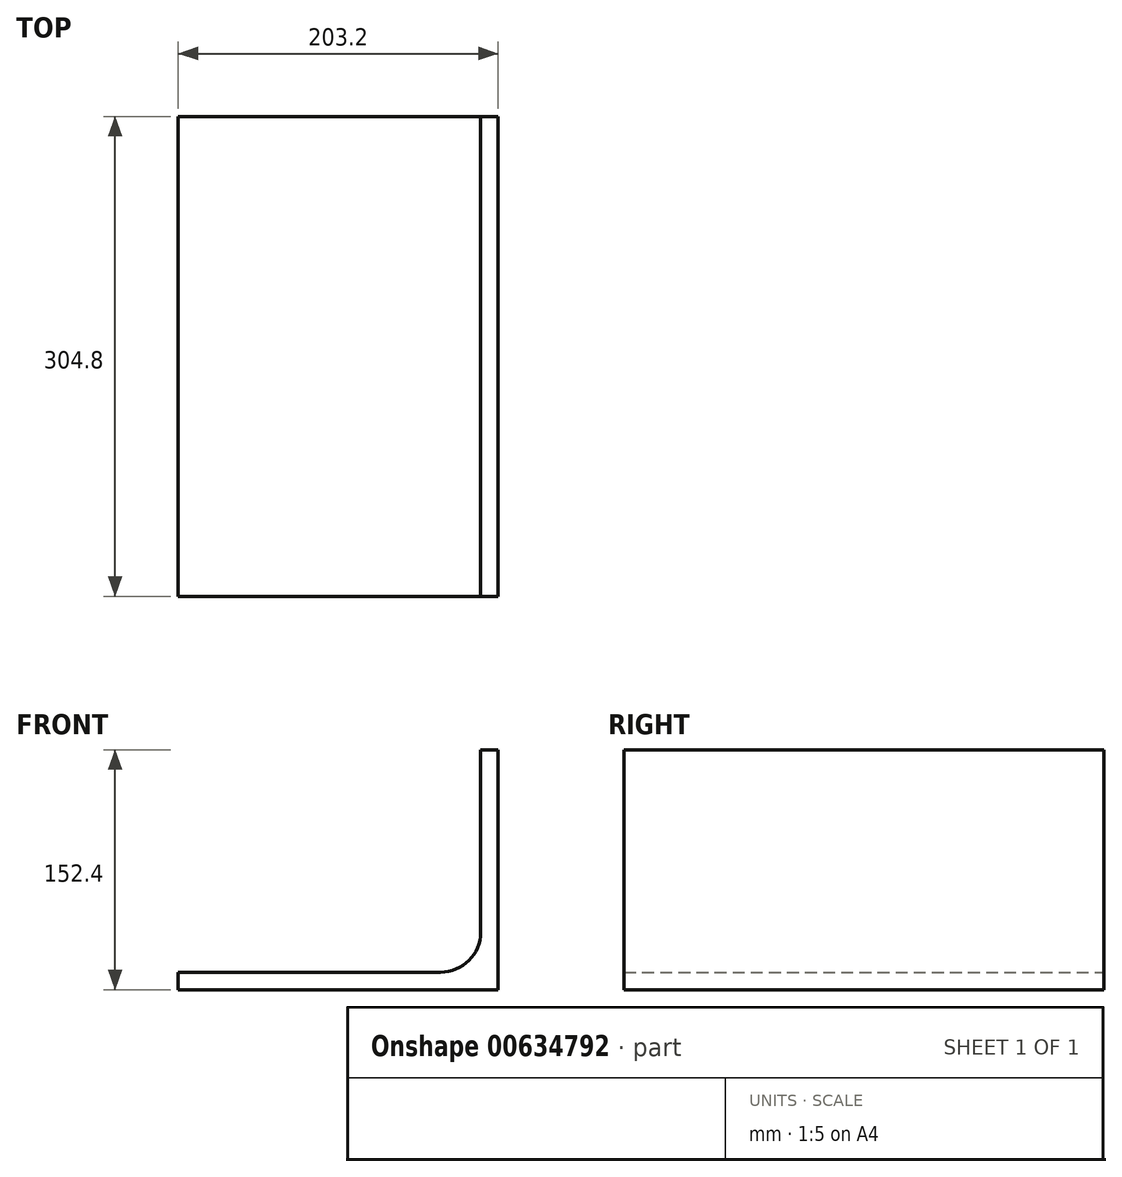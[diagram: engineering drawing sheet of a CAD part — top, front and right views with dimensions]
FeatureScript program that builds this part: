
annotation { "Feature Type Name" : "Feature", "Feature Type Description" : "" }
export const myFeature = defineFeature(function(context is Context, id is Id, definition is map)
    precondition{}
    {
        {
            var Q0;
            Q0=qCreatedBy(makeId("Front.planeOp"),FACE);
            var sketch = newSketch(context, id + "F0", { "sketchPlane" : qUnion([Q0])});
            skLineSegment(sketch, "E0.bottom", {"start": v(-101.6, 5.56) * mm, "end": v(65.09, 5.56) * mm});
            skLineSegment(sketch, "E0.top", {"start": v(-101.6, -5.56) * mm, "end": v(101.6, -5.56) * mm});
            skLineSegment(sketch, "E0.left", {"start": v(-101.6, 5.56) * mm, "end": v(-101.6, -5.56) * mm});
            skLineSegment(sketch, "E0.right", {"start": v(101.6, 146.84) * mm, "end": v(101.6, -5.56) * mm});
            skLineSegment(sketch, "E1", {"start": v(-101.6, 5.56) * mm, "end": v(101.6, -5.56) * mm, "construction": true});
            skLineSegment(sketch, "E2", {"start": v(101.6, 146.84) * mm, "end": v(90.49, 146.84) * mm});
            skLineSegment(sketch, "E3", {"start": v(90.49, 146.84) * mm, "end": v(90.49, 30.96) * mm});
            skPoint(sketch, "E4.visualSharp", {"position": v(90.49, 5.56) * mm});
            skArc(sketch, "E4.filletArc", {"start": v(65.09, 5.56) * mm, "mid": v(83.05, 13) * mm, "end": v(90.49, 30.96) * mm});
            skSolve(sketch);
        }
        {
            var Q0;
            Q0=qSketchRegion(id+"F0",true);
            extrude(context, id + "F1", {"entities" : qUnion([Q0]), "endBound" : BoundingType.SYMMETRIC, "depth" : 304.8 * mm, "offsetDistance" : 25.4 * mm});
        }
    });
